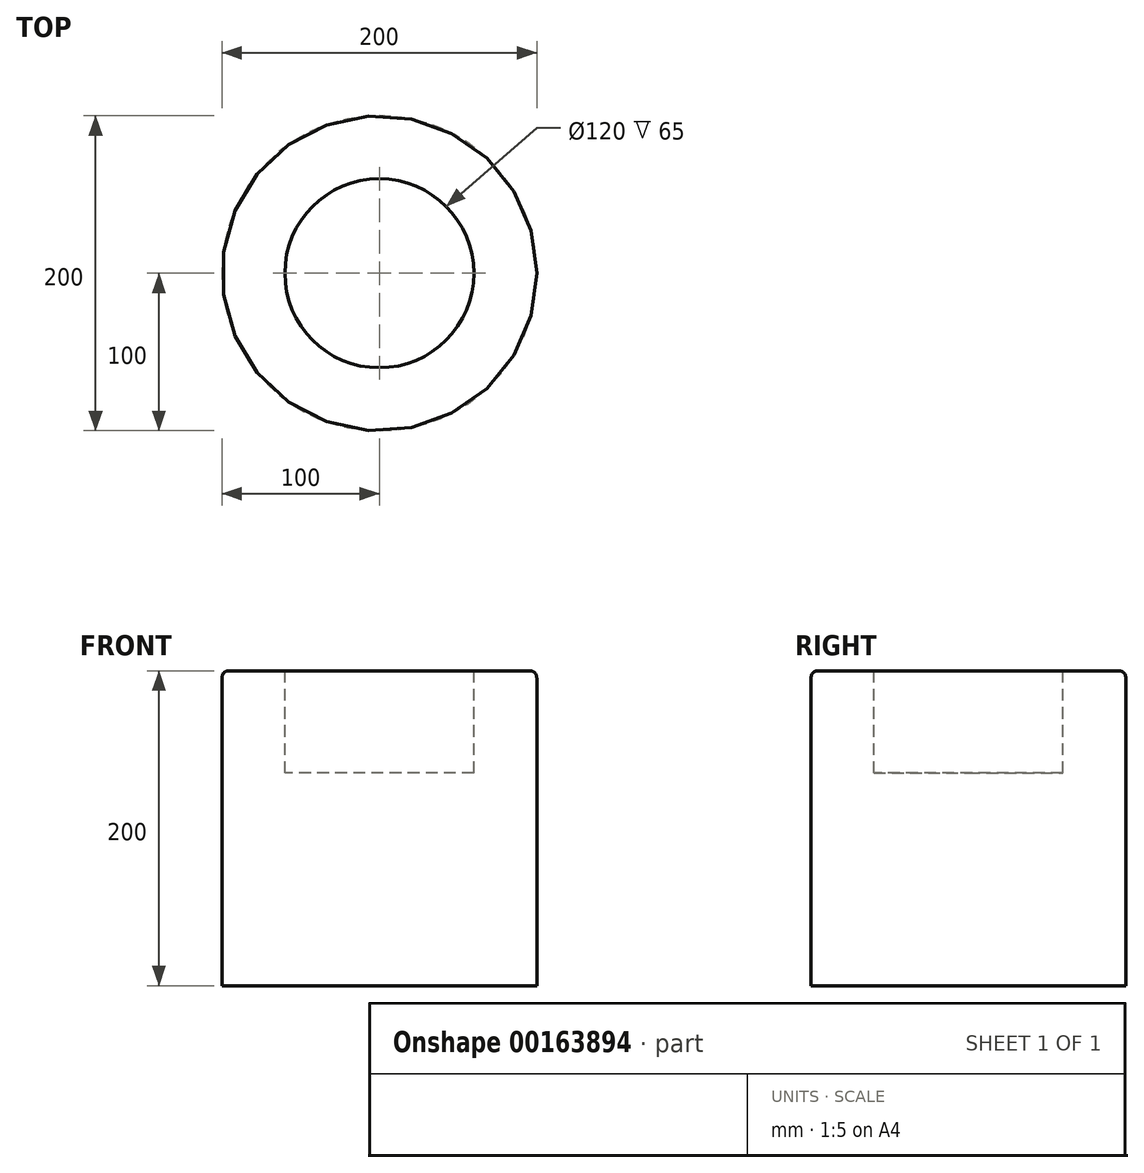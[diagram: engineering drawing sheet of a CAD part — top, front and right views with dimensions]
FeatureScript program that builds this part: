
annotation { "Feature Type Name" : "Feature", "Feature Type Description" : "" }
export const myFeature = defineFeature(function(context is Context, id is Id, definition is map)
    precondition{}
    {
        {
            var Q0;
            Q0=qCreatedBy(makeId("Top.planeOp"),FACE);
            var sketch = newSketch(context, id + "F0", { "sketchPlane" : qUnion([Q0])});
            skCircle(sketch, "E0", {"center": v(0, 0) * mm, "radius": 100 * mm});
            skSolve(sketch);
        }
        {
            var Q0;
            Q0=makeQuery(id+"F0.imprint","IMPRINT",FACE,{"disambiguationData":[TD([[makeQuery(id+"F0.imprint","IMPRINT",EDGE,{"derivedFrom":sQuery(id+"F0.wireOp",EDGE,"E0")}),1.0]])]});
            extrude(context, id + "F1", {"entities" : qUnion([Q0]), "depth" : 200 * mm});
        }
        {
            var Q0;
            Q0=makeQuery(id+"F1.opExtrude","CAP_FACE",FACE,{"disambiguationData":[OSD([sQuery(id+"F0.wireOp",EDGE,"E0")])],"isStart":false});
            var sketch = newSketch(context, id + "F4", { "sketchPlane" : qUnion([Q0])});
            skCircle(sketch, "E1", {"center": v(0, 0) * mm, "radius": 60 * mm});
            skSolve(sketch);
        }
        {
            var Q0;
            Q0=makeQuery(id+"F4.imprint","IMPRINT",FACE,{"disambiguationData":[TD([[makeQuery(id+"F4.imprint","IMPRINT",EDGE,{"derivedFrom":sQuery(id+"F4.wireOp",EDGE,"E1")}),1.0]])]});
            extrude(context, id + "F2", {"entities" : qUnion([Q0]), "operationType" : NewBodyOperationType.REMOVE, "oppositeDirection" : true, "depth" : 65 * mm});
        }
        {
            var Q0;
            Q0=makeQuery(id+"F1.opExtrude","CAP_EDGE",EDGE,{"disambiguationData":[OSD([sQuery(id+"F0.wireOp",EDGE,"E0")])],"isStart":false});
            var Q1;
            Q1=makeQuery(id+"F2.boolean.opBoolean","COPY",EDGE,{"derivedFrom":makeQuery(id+"F2.opExtrude","CAP_EDGE",EDGE,{"disambiguationData":[OSD([sQuery(id+"F4.wireOp",EDGE,"E1")])],"isStart":true})});
            fillet(context, id + "F3", {"entities" : qUnion([Q0, Q1]), "radius" : 5 * mm, "rho" : 0.5, "crossSection" : FilletCrossSection.CONIC, "allowEdgeOverflow" : false});
        }
    });
